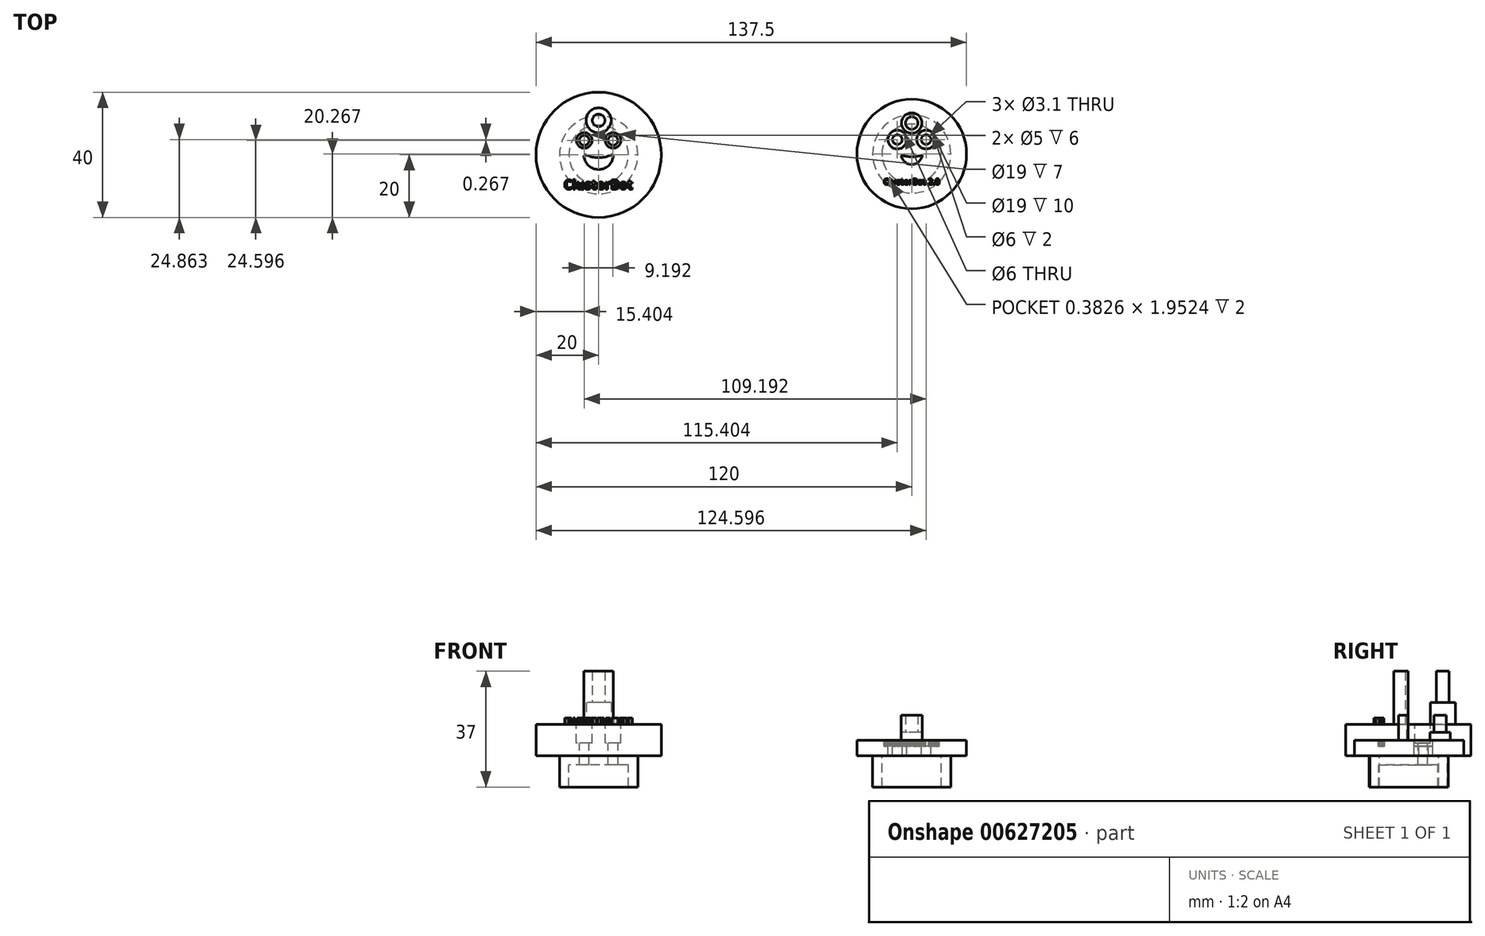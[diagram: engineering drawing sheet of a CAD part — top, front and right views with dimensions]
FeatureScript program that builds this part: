
annotation { "Feature Type Name" : "Feature", "Feature Type Description" : "" }
export const myFeature = defineFeature(function(context is Context, id is Id, definition is map)
    precondition{}
    {
        {
            var Q0;
            Q0=qCreatedBy(makeId("Top.planeOp"),FACE);
            var sketch = newSketch(context, id + "F0", { "sketchPlane" : qUnion([Q0])});
            skCircle(sketch, "E0", {"center": v(0, 0) * mm, "radius": 20 * mm});
            skLineSegment(sketch, "E1", {"start": v(0, 57.86) * mm, "end": v(0, -51.25) * mm, "construction": true});
            skLineSegment(sketch, "E2", {"start": v(-57.98, 0) * mm, "end": v(50.32, 0) * mm, "construction": true});
            skCircle(sketch, "E3", {"center": v(0, 11) * mm, "radius": 2 * mm});
            skCircle(sketch, "E4", {"center": v(0, 0) * mm, "radius": 4.7 * mm});
            skLineSegment(sketch, "E5", {"start": v(0, 11) * mm, "end": v(0, 0) * mm});
            skLineSegment(sketch, "E6", {"start": v(0, 36.77) * mm, "end": v(-4.7, 0.27) * mm, "construction": true});
            skCircle(sketch, "E7", {"center": v(0, 0) * mm, "radius": 9.5 * mm});
            skCircle(sketch, "E8", {"center": v(0, 0) * mm, "radius": 12.5 * mm});
            skArc(sketch, "E9", {"start": v(-4.7, 0.27) * mm, "mid": v(0, -0.9) * mm, "end": v(4.7, 0.27) * mm});
            skLineSegment(sketch, "E10", {"start": v(50, 46.01) * mm, "end": v(50, -53.99) * mm, "construction": true});
            skCircle(sketch, "E11", {"center": v(100, 0.27) * mm, "radius": 9.5 * mm});
            skCircle(sketch, "E12", {"center": v(100, 0.27) * mm, "radius": 12.5 * mm});
            skLineSegment(sketch, "E13", {"start": v(100, 0.27) * mm, "end": v(100, 40.45) * mm, "construction": true});
            skCircle(sketch, "E14", {"center": v(100, 10.14) * mm, "radius": 2 * mm});
            skCircle(sketch, "E15", {"center": v(100, 0.27) * mm, "radius": 17.5 * mm});
            skCircle(sketch, "E16", {"center": v(100, 0.27) * mm, "radius": 3.37 * mm});
            skLineSegment(sketch, "E17", {"start": v(96.65, -0.12) * mm, "end": v(103.35, -0.12) * mm});
            skArc(sketch, "E18", {"start": v(96.65, -0.12) * mm, "mid": v(100, -0.6) * mm, "end": v(103.35, -0.12) * mm});
            skSolve(sketch);
        }
        {
            var Q0;
            Q0=makeQuery(id+"F0.imprint","IMPRINT",FACE,{"disambiguationData":[TD([[makeQuery(id+"F0.imprint","IMPRINT",EDGE,{"derivedFrom":sQuery(id+"F0.wireOp",EDGE,"E0")}),1.0]])]});
            var Q1;
            {var subQ0=sQuery(id+"F0.wireOp",EDGE,"EMk8Hpbs-Uu9s-4hnP-Wr23-4mz9YGDRhDCW");var subQ1=sQuery(id+"F0.wireOp",EDGE,"E4");var subQ2=makeQuery(id+"F0.imprint","INTERSECT",VERTEX,{"disambiguationData":[OD(0.0)],"derivedFrom":[subQ1,subQ0]});Q1=makeQuery(id+"F0.imprint","IMPRINT",FACE,{"disambiguationData":[TD([[makeQuery(id+"F0.imprint","IMPRINT",EDGE,{"disambiguationData":[TD([[subQ2,1.0]])],"derivedFrom":subQ1}),1.0]])]});}
            var Q2;
            {var subQ0=sQuery(id+"F0.wireOp",EDGE,"EMk8Hpbs-Uu9s-4hnP-Wr23-4mz9YGDRhDCW");var subQ1=sQuery(id+"F0.wireOp",EDGE,"E4");var subQ2=makeQuery(id+"F0.imprint","INTERSECT",VERTEX,{"disambiguationData":[OD(1.0)],"derivedFrom":[subQ1,subQ0]});Q2=makeQuery(id+"F0.imprint","IMPRINT",FACE,{"disambiguationData":[TD([[makeQuery(id+"F0.imprint","IMPRINT",EDGE,{"disambiguationData":[TD([[subQ2,-1.0]])],"derivedFrom":subQ1}),1.0]])]});}
            var Q3;
            {var subQ3=sQuery(id+"F0.wireOp",EDGE,"E5");var subQ6=sQuery(id+"F0.wireOp",EDGE,"E3");var subQ7=makeQuery(id+"F0.imprint","INTERSECT",VERTEX,{"derivedFrom":[subQ6,subQ3]});Q3=makeQuery(id+"F0.imprint","IMPRINT",FACE,{"disambiguationData":[TD([[makeQuery(id+"F0.imprint","IMPRINT",EDGE,{"disambiguationData":[TD([[subQ7,1.0]])],"derivedFrom":subQ6}),-1.0]])]});}
            extrude(context, id + "F1", {"entities" : qUnion([Q0, Q1, Q2, Q3]), "depth" : 10 * mm, "offsetDistance" : 25 * mm});
        }
        {
            var Q0;
            Q0=makeQuery(id+"F0.imprint","IMPRINT",FACE,{"disambiguationData":[TD([[makeQuery(id+"F0.imprint","IMPRINT",EDGE,{"derivedFrom":sQuery(id+"F0.wireOp",EDGE,"E3")}),1.0]])]});
            var Q1;
            {var subQ0=sQuery(id+"F0.wireOp",EDGE,"EMk8Hpbs-Uu9s-4hnP-Wr23-4mz9YGDRhDCW");var subQ1=sQuery(id+"F0.wireOp",EDGE,"E4");var subQ2=makeQuery(id+"F0.imprint","INTERSECT",VERTEX,{"disambiguationData":[OD(0.0)],"derivedFrom":[subQ1,subQ0]});Q1=makeQuery(id+"F0.imprint","IMPRINT",FACE,{"disambiguationData":[TD([[makeQuery(id+"F0.imprint","IMPRINT",EDGE,{"disambiguationData":[TD([[subQ2,-1.0]])],"derivedFrom":subQ1}),1.0]])]});}
            var Q2;
            {var subQ0=sQuery(id+"F0.wireOp",EDGE,"E8");var subQ1=sQuery(id+"F0.wireOp",EDGE,"E3");var subQ2=makeQuery(id+"F0.imprint","INTERSECT",VERTEX,{"disambiguationData":[OD(0.0)],"derivedFrom":[subQ1,subQ0]});Q2=makeQuery(id+"F0.imprint","IMPRINT",FACE,{"disambiguationData":[TD([[makeQuery(id+"F0.imprint","IMPRINT",EDGE,{"disambiguationData":[TD([[subQ2,1.0]])],"derivedFrom":subQ1}),1.0]])]});}
            var Q3;
            {var subQ0=sQuery(id+"F0.wireOp",EDGE,"E5");var subQ1=sQuery(id+"F0.wireOp",EDGE,"E3");var subQ2=makeQuery(id+"F0.imprint","INTERSECT",VERTEX,{"derivedFrom":[subQ1,subQ0]});Q3=makeQuery(id+"F0.imprint","IMPRINT",FACE,{"disambiguationData":[TD([[makeQuery(id+"F0.imprint","IMPRINT",EDGE,{"disambiguationData":[TD([[subQ2,-1.0]])],"derivedFrom":subQ1}),1.0]])]});}
            var Q4;
            {var subQ0=sQuery(id+"F0.wireOp",EDGE,"E5");var subQ1=sQuery(id+"F0.wireOp",EDGE,"E3");var subQ2=makeQuery(id+"F0.imprint","INTERSECT",VERTEX,{"derivedFrom":[subQ1,subQ0]});Q4=makeQuery(id+"F0.imprint","IMPRINT",FACE,{"disambiguationData":[TD([[makeQuery(id+"F0.imprint","IMPRINT",EDGE,{"disambiguationData":[TD([[subQ2,1.0]])],"derivedFrom":subQ1}),1.0]])]});}
            extrude(context, id + "F2", {"entities" : qUnion([Q0, Q1, Q2, Q3, Q4]), "operationType" : NewBodyOperationType.ADD, "depth" : 27 * mm, "offsetDistance" : 25 * mm});
        }
        {
            var Q0;
            {var subQ0=sQuery(id+"F0.wireOp",EDGE,"E8");var subQ1=sQuery(id+"F0.wireOp",EDGE,"E3");var subQ2=makeQuery(id+"F0.imprint","INTERSECT",VERTEX,{"disambiguationData":[OD(0.0)],"derivedFrom":[subQ1,subQ0]});Q0=makeQuery(id+"F0.imprint","IMPRINT",FACE,{"disambiguationData":[TD([[makeQuery(id+"F0.imprint","IMPRINT",EDGE,{"disambiguationData":[TD([[subQ2,-1.0]])],"derivedFrom":subQ1}),-1.0]])]});}
            extrude(context, id + "F3", {"entities" : qUnion([Q0]), "operationType" : NewBodyOperationType.ADD, "oppositeDirection" : true, "depth" : 10 * mm, "offsetDistance" : 25 * mm, "hasSecondDirection" : true, "secondDirectionOppositeDirection" : false, "secondDirectionDepth" : 10 * mm});
        }
        {
            var Q0;
            {var subQ2=sQuery(id+"F0.wireOp",EDGE,"E3");var subQ5=sQuery(id+"F0.wireOp",EDGE,"E8");var subQ6=makeQuery(id+"F0.imprint","INTERSECT",VERTEX,{"disambiguationData":[OD(0.0)],"derivedFrom":[subQ2,subQ5]});Q0=makeQuery(id+"F0.imprint","IMPRINT",FACE,{"disambiguationData":[TD([[makeQuery(id+"F0.imprint","IMPRINT",EDGE,{"disambiguationData":[TD([[subQ6,-1.0]])],"derivedFrom":subQ2}),1.0]])]});}
            extrude(context, id + "F4", {"entities" : qUnion([Q0]), "operationType" : NewBodyOperationType.ADD, "oppositeDirection" : true, "depth" : 10 * mm, "offsetDistance" : 25 * mm});
        }
        {
            var Q0;
            {var subQ0=sQuery(id+"F0.wireOp",EDGE,"E9");var subQ1=sQuery(id+"F0.wireOp",EDGE,"E4");Q0=makeQuery(id+"F2.opExtrude","SWEPT_EDGE",EDGE,{"disambiguationData":[OSD([subQ1,subQ0]),TDD([makeQuery(id+"F0.imprint","INTERSECT",VERTEX,{"disambiguationData":[OD(1.0)],"derivedFrom":[subQ1,subQ0]})])]});}
            var Q1;
            {var subQ0=sQuery(id+"F0.wireOp",EDGE,"E9");var subQ1=sQuery(id+"F0.wireOp",EDGE,"E4");Q1=makeQuery(id+"F2.opExtrude","SWEPT_EDGE",EDGE,{"disambiguationData":[OSD([subQ1,subQ0]),TDD([makeQuery(id+"F0.imprint","INTERSECT",VERTEX,{"disambiguationData":[OD(0.0)],"derivedFrom":[subQ1,subQ0]})])]});}
            fillet(context, id + "F5", {"entities" : qUnion([Q0, Q1]), "radius" : 0.5 * mm, "tangentPropagation" : true, "allowEdgeOverflow" : false});
        }
        {
            var Q0;
            {var subQ0=sQuery(id+"F0.wireOp",EDGE,"E8");var subQ1=sQuery(id+"F0.wireOp",EDGE,"E7");var subQ2=sQuery(id+"F0.wireOp",EDGE,"E3");Q0=makeQuery(id+"F3.boolean.opBoolean","MERGE",FACE,{"derivedFrom":[makeQuery(id+"F1.opExtrude","CAP_FACE",FACE,{"disambiguationData":[OSD([sQuery(id+"F0.wireOp",EDGE,"E0"),subQ2,subQ0])],"isStart":false}),makeQuery(id+"F1.opExtrude","CAP_FACE",FACE,{"disambiguationData":[OSD([subQ2,sQuery(id+"F0.wireOp",EDGE,"E4"),subQ1,sQuery(id+"F0.wireOp",EDGE,"E9")])],"isStart":false}),makeQuery(id+"F3.opExtrude","CAP_FACE",FACE,{"disambiguationData":[OSD([subQ2,subQ1,subQ0])],"isStart":true})]});}
            var sketch = newSketch(context, id + "F6", { "sketchPlane" : qUnion([Q0])});
            skLineSegment(sketch, "E19", {"start": v(0, 0) * mm, "end": v(-10.6, 10.6) * mm, "construction": true});
            skLineSegment(sketch, "E20", {"start": v(0, 0) * mm, "end": v(10.6, 10.6) * mm, "construction": true});
            skCircle(sketch, "E21", {"center": v(4.6, 4.6) * mm, "radius": 1.55 * mm});
            skCircle(sketch, "E22", {"center": v(4.6, 4.6) * mm, "radius": 2.5 * mm});
            skCircle(sketch, "E23", {"center": v(-4.6, 4.6) * mm, "radius": 1.55 * mm});
            skCircle(sketch, "E24", {"center": v(-4.6, 4.6) * mm, "radius": 2.5 * mm});
            skSolve(sketch);
        }
        {
            var Q0;
            Q0=makeQuery(id+"F6.imprint","IMPRINT",FACE,{"disambiguationData":[TD([[makeQuery(id+"F6.imprint","IMPRINT",EDGE,{"derivedFrom":sQuery(id+"F6.wireOp",EDGE,"E23")}),1.0]])]});
            var Q1;
            Q1=makeQuery(id+"F6.imprint","IMPRINT",FACE,{"disambiguationData":[TD([[makeQuery(id+"F6.imprint","IMPRINT",EDGE,{"derivedFrom":sQuery(id+"F6.wireOp",EDGE,"E21")}),1.0]])]});
            extrude(context, id + "F7", {"entities" : qUnion([Q0, Q1]), "operationType" : NewBodyOperationType.REMOVE, "oppositeDirection" : true, "depth" : 10 * mm, "offsetDistance" : 25 * mm});
        }
        {
            var Q0;
            Q0=makeQuery(id+"F6.imprint","IMPRINT",FACE,{"disambiguationData":[TD([[makeQuery(id+"F6.imprint","IMPRINT",EDGE,{"derivedFrom":sQuery(id+"F6.wireOp",EDGE,"E21")}),-1.0]])]});
            var Q1;
            Q1=makeQuery(id+"F6.imprint","IMPRINT",FACE,{"disambiguationData":[TD([[makeQuery(id+"F6.imprint","IMPRINT",EDGE,{"derivedFrom":sQuery(id+"F6.wireOp",EDGE,"E23")}),-1.0]])]});
            extrude(context, id + "F8", {"entities" : qUnion([Q0, Q1]), "operationType" : NewBodyOperationType.REMOVE, "oppositeDirection" : true, "depth" : 6 * mm, "offsetDistance" : 25 * mm});
        }
        {
            var Q0;
            {var subQ0=sQuery(id+"F0.wireOp",EDGE,"E8");var subQ1=sQuery(id+"F0.wireOp",EDGE,"E7");var subQ2=sQuery(id+"F0.wireOp",EDGE,"E3");Q0=makeQuery(id+"F3.boolean.opBoolean","MERGE",FACE,{"derivedFrom":[makeQuery(id+"F1.opExtrude","CAP_FACE",FACE,{"disambiguationData":[OSD([sQuery(id+"F0.wireOp",EDGE,"E0"),subQ2,subQ0])],"isStart":false}),makeQuery(id+"F1.opExtrude","CAP_FACE",FACE,{"disambiguationData":[OSD([subQ2,sQuery(id+"F0.wireOp",EDGE,"E4"),subQ1,sQuery(id+"F0.wireOp",EDGE,"E9")])],"isStart":false}),makeQuery(id+"F3.opExtrude","CAP_FACE",FACE,{"disambiguationData":[OSD([subQ2,subQ1,subQ0])],"isStart":true})]});}
            var sketch = newSketch(context, id + "F9", { "sketchPlane" : qUnion([Q0])});
            skText(sketch, "E25", { "text": "ClusterBot", "fontName": "OpenSans-Bold.ttf"});
            const initialGuessF9  = {"E25": [-0.01111, -0.011, 1, 0, 0.003]};
            skSetInitialGuess(sketch, initialGuessF9);
            skSolve(sketch);
        }
        {
            var Q0;
            Q0=qSketchRegion(id+"F9",true);
            extrude(context, id + "F10", {"entities" : qUnion([Q0]), "operationType" : NewBodyOperationType.ADD, "depth" : 2 * mm, "offsetDistance" : 25 * mm});
        }
        {
            var Q0;
            {var subQ0=sQuery(id+"F0.wireOp",EDGE,"E9");var subQ1=sQuery(id+"F0.wireOp",EDGE,"E4");var subQ2=sQuery(id+"F0.wireOp",EDGE,"E3");var subQ3=sQuery(id+"F0.wireOp",EDGE,"E0");var subQ4=sQuery(id+"F0.wireOp",EDGE,"E8");var subQ5=sQuery(id+"F0.wireOp",EDGE,"E7");Q0=makeQuery(id+"F10.boolean.opBoolean","SPLIT",FACE,{"disambiguationData":[TD([makeQuery(id+"F1.opExtrude","SWEPT_FACE",FACE,{"disambiguationData":[OSD([subQ3])]})])],"derivedFrom":makeQuery(id+"F3.boolean.opBoolean","MERGE",FACE,{"derivedFrom":[makeQuery(id+"F1.opExtrude","CAP_FACE",FACE,{"disambiguationData":[OSD([subQ3,subQ2,subQ4])],"isStart":false}),makeQuery(id+"F1.opExtrude","CAP_FACE",FACE,{"disambiguationData":[OSD([subQ2,subQ1,subQ5,subQ0])],"isStart":false}),makeQuery(id+"F3.opExtrude","CAP_FACE",FACE,{"disambiguationData":[OSD([subQ2,subQ5,subQ4])],"isStart":true})]})});}
            var sketch = newSketch(context, id + "F11", { "sketchPlane" : qUnion([Q0])});
            skCircle(sketch, "E26", {"center": v(0, 11) * mm, "radius": 4 * mm});
            skSolve(sketch);
        }
        {
            var Q0;
            Q0=qSketchRegion(id+"F11",true);
            extrude(context, id + "F12", {"entities" : qUnion([Q0]), "operationType" : NewBodyOperationType.ADD, "depth" : 7 * mm, "offsetDistance" : 25 * mm});
        }
        {
            var Q0;
            {var subQ0=sQuery(id+"F0.wireOp",EDGE,"E7");var subQ1=sQuery(id+"F0.wireOp",EDGE,"E9");var subQ2=sQuery(id+"F0.wireOp",EDGE,"E4");var subQ3=sQuery(id+"F0.wireOp",EDGE,"E3");Q0=makeQuery(id+"F4.boolean.opBoolean","SPLIT",FACE,{"disambiguationData":[TD([makeQuery(id+"F3.opExtrude","SWEPT_FACE",FACE,{"disambiguationData":[OSD([subQ0])]})])],"derivedFrom":makeQuery(id+"F2.boolean.opBoolean","MERGE",FACE,{"derivedFrom":[makeQuery(id+"F1.opExtrude","CAP_FACE",FACE,{"disambiguationData":[OSD([sQuery(id+"F0.wireOp",EDGE,"E0"),subQ3,sQuery(id+"F0.wireOp",EDGE,"E8")])],"isStart":true}),makeQuery(id+"F1.opExtrude","CAP_FACE",FACE,{"disambiguationData":[OSD([subQ3,subQ2,subQ0,subQ1])],"isStart":true}),makeQuery(id+"F2.opExtrude","CAP_FACE",FACE,{"disambiguationData":[OSD([subQ3])],"isStart":true}),makeQuery(id+"F2.opExtrude","CAP_FACE",FACE,{"disambiguationData":[OSD([subQ2,subQ1])],"isStart":true})]})});}
            extrude(context, id + "F13", {"entities" : qUnion([Q0]), "operationType" : NewBodyOperationType.ADD, "depth" : 3 * mm, "offsetDistance" : 25 * mm});
        }
        {
            var Q0;
            Q0=makeQuery(id+"F0.imprint","IMPRINT",FACE,{"disambiguationData":[TD([[makeQuery(id+"F0.imprint","IMPRINT",EDGE,{"derivedFrom":sQuery(id+"F0.wireOp",EDGE,"E12")}),-1.0]])]});
            var Q1;
            Q1=makeQuery(id+"F0.imprint","IMPRINT",FACE,{"disambiguationData":[TD([[makeQuery(id+"F0.imprint","IMPRINT",EDGE,{"derivedFrom":sQuery(id+"F0.wireOp",EDGE,"E12")}),1.0]])]});
            var Q2;
            {var subQ0=sQuery(id+"F0.wireOp",EDGE,"E14");var subQ1=sQuery(id+"F0.wireOp",EDGE,"E11");var subQ2=makeQuery(id+"F0.imprint","INTERSECT",VERTEX,{"disambiguationData":[OD(0.0)],"derivedFrom":[subQ1,subQ0]});Q2=makeQuery(id+"F0.imprint","IMPRINT",FACE,{"disambiguationData":[TD([[makeQuery(id+"F0.imprint","IMPRINT",EDGE,{"disambiguationData":[TD([[subQ2,-1.0]])],"derivedFrom":subQ1}),1.0]])]});}
            var Q3;
            {var subQ0=sQuery(id+"F0.wireOp",EDGE,"INGHYkTo-cHFD-LJoG-0GR1-I3Dc0VJQrvcC");Q3=makeQuery(id+"F0.imprint","IMPRINT",FACE,{"disambiguationData":[TD([[makeQuery(id+"F0.imprint","IMPRINT",EDGE,{"derivedFrom":subQ0}),1.0]])]});}
            var Q4;
            {var subQ0=sQuery(id+"F0.wireOp",EDGE,"hYN0OAPL-6847-LTPc-NbCf-sZvM7d4d9N3J");Q4=makeQuery(id+"F0.imprint","IMPRINT",FACE,{"disambiguationData":[TD([[makeQuery(id+"F0.imprint","IMPRINT",EDGE,{"derivedFrom":subQ0}),1.0]])]});}
            var Q5;
            {var subQ1=sQuery(id+"F0.wireOp",EDGE,"E17");Q5=makeQuery(id+"F0.imprint","IMPRINT",FACE,{"disambiguationData":[TD([[makeQuery(id+"F0.imprint","IMPRINT",EDGE,{"derivedFrom":subQ1}),1.0]])]});}
            var Q6;
            Q6=makeQuery(id+"F0.imprint","IMPRINT",FACE,{"disambiguationData":[TD([[makeQuery(id+"F0.imprint","IMPRINT",EDGE,{"derivedFrom":sQuery(id+"F0.wireOp",EDGE,"E17")}),-1.0]])]});
            extrude(context, id + "F14", {"entities" : qUnion([Q0, Q1, Q2, Q3, Q4, Q5, Q6]), "depth" : 5 * mm, "offsetDistance" : 25 * mm});
        }
        {
            var Q0;
            {var subQ0=sQuery(id+"F0.wireOp",EDGE,"E14");var subQ1=sQuery(id+"F0.wireOp",EDGE,"E11");var subQ2=makeQuery(id+"F0.imprint","INTERSECT",VERTEX,{"disambiguationData":[OD(0.0)],"derivedFrom":[subQ1,subQ0]});Q0=makeQuery(id+"F0.imprint","IMPRINT",FACE,{"disambiguationData":[TD([[makeQuery(id+"F0.imprint","IMPRINT",EDGE,{"disambiguationData":[TD([[subQ2,1.0]])],"derivedFrom":subQ1}),-1.0]])]});}
            var Q1;
            {var subQ0=sQuery(id+"F0.wireOp",EDGE,"E14");var subQ1=sQuery(id+"F0.wireOp",EDGE,"E11");var subQ2=makeQuery(id+"F0.imprint","INTERSECT",VERTEX,{"disambiguationData":[OD(0.0)],"derivedFrom":[subQ1,subQ0]});Q1=makeQuery(id+"F0.imprint","IMPRINT",FACE,{"disambiguationData":[TD([[makeQuery(id+"F0.imprint","IMPRINT",EDGE,{"disambiguationData":[TD([[subQ2,1.0]])],"derivedFrom":subQ1}),1.0]])]});}
            var Q2;
            {var subQ0=sQuery(id+"F0.wireOp",EDGE,"hYN0OAPL-6847-LTPc-NbCf-sZvM7d4d9N3J");Q2=makeQuery(id+"F0.imprint","IMPRINT",FACE,{"disambiguationData":[TD([[makeQuery(id+"F0.imprint","IMPRINT",EDGE,{"derivedFrom":subQ0}),-1.0]])]});}
            var Q3;
            {var subQ0=sQuery(id+"F0.wireOp",EDGE,"E18");Q3=makeQuery(id+"F0.imprint","IMPRINT",FACE,{"disambiguationData":[TD([[makeQuery(id+"F0.imprint","IMPRINT",EDGE,{"derivedFrom":subQ0}),-1.0]])]});}
            extrude(context, id + "F15", {"entities" : qUnion([Q0, Q1, Q2, Q3]), "operationType" : NewBodyOperationType.ADD, "depth" : 13 * mm, "offsetDistance" : 25 * mm});
        }
        {
            var Q0;
            Q0=makeQuery(id+"F0.imprint","IMPRINT",FACE,{"disambiguationData":[TD([[makeQuery(id+"F0.imprint","IMPRINT",EDGE,{"derivedFrom":sQuery(id+"F0.wireOp",EDGE,"E12")}),1.0]])]});
            var Q1;
            {var subQ0=sQuery(id+"F0.wireOp",EDGE,"E14");var subQ1=sQuery(id+"F0.wireOp",EDGE,"E11");var subQ2=makeQuery(id+"F0.imprint","INTERSECT",VERTEX,{"disambiguationData":[OD(0.0)],"derivedFrom":[subQ1,subQ0]});Q1=makeQuery(id+"F0.imprint","IMPRINT",FACE,{"disambiguationData":[TD([[makeQuery(id+"F0.imprint","IMPRINT",EDGE,{"disambiguationData":[TD([[subQ2,1.0]])],"derivedFrom":subQ1}),-1.0]])]});}
            extrude(context, id + "F16", {"entities" : qUnion([Q0, Q1]), "operationType" : NewBodyOperationType.ADD, "oppositeDirection" : true, "depth" : 10 * mm, "offsetDistance" : 25 * mm});
        }
        {
            var Q0;
            Q0=makeQuery(id+"F14.opExtrude","CAP_FACE",FACE,{"disambiguationData":[OSD([sQuery(id+"F0.wireOp",EDGE,"E14"),sQuery(id+"F0.wireOp",EDGE,"E15"),sQuery(id+"F0.wireOp",EDGE,"E16"),sQuery(id+"F0.wireOp",EDGE,"INGHYkTo-cHFD-LJoG-0GR1-I3Dc0VJQrvcC")])],"isStart":false});
            var sketch = newSketch(context, id + "F17", { "sketchPlane" : qUnion([Q0])});
            skLineSegment(sketch, "E27", {"start": v(100, 0.27) * mm, "end": v(108.49, 8.75) * mm, "construction": true});
            skLineSegment(sketch, "E28", {"start": v(100, 0.27) * mm, "end": v(91.51, 8.75) * mm, "construction": true});
            skCircle(sketch, "E29", {"center": v(104.6, 4.86) * mm, "radius": 1.55 * mm});
            skCircle(sketch, "E30", {"center": v(104.6, 4.86) * mm, "radius": 3 * mm});
            skLineSegment(sketch, "E31", {"start": v(100, 0.27) * mm, "end": v(100, 10.14) * mm, "construction": true});
            skCircle(sketch, "E32.MirrorC", {"center": v(95.4, 4.86) * mm, "radius": 1.55 * mm});
            skCircle(sketch, "E33.MirrorC", {"center": v(95.4, 4.86) * mm, "radius": 3 * mm});
            skCircle(sketch, "E34", {"center": v(100, 10.14) * mm, "radius": 3.25 * mm});
            skSolve(sketch);
        }
        {
            var Q0;
            Q0=makeQuery(id+"F17.imprint","IMPRINT",FACE,{"disambiguationData":[TD([[makeQuery(id+"F17.imprint","IMPRINT",EDGE,{"derivedFrom":sQuery(id+"F17.wireOp",EDGE,"E32.MirrorC")}),1.0]])]});
            var Q1;
            Q1=makeQuery(id+"F17.imprint","IMPRINT",FACE,{"disambiguationData":[TD([[makeQuery(id+"F17.imprint","IMPRINT",EDGE,{"derivedFrom":sQuery(id+"F17.wireOp",EDGE,"E29")}),-1.0]])]});
            extrude(context, id + "F18", {"entities" : qUnion([Q0, Q1]), "operationType" : NewBodyOperationType.REMOVE, "oppositeDirection" : true, "depth" : 2 * mm, "offsetDistance" : 25 * mm});
        }
        {
            var Q0;
            Q0=makeQuery(id+"F17.imprint","IMPRINT",FACE,{"disambiguationData":[TD([[makeQuery(id+"F17.imprint","IMPRINT",EDGE,{"derivedFrom":sQuery(id+"F17.wireOp",EDGE,"E32.MirrorC")}),-1.0]])]});
            var Q1;
            Q1=makeQuery(id+"F17.imprint","IMPRINT",FACE,{"disambiguationData":[TD([[makeQuery(id+"F17.imprint","IMPRINT",EDGE,{"derivedFrom":sQuery(id+"F17.wireOp",EDGE,"E29")}),1.0]])]});
            extrude(context, id + "F19", {"entities" : qUnion([Q0, Q1]), "operationType" : NewBodyOperationType.REMOVE, "oppositeDirection" : true, "depth" : 10 * mm, "offsetDistance" : 25 * mm});
        }
        {
            var Q0;
            {var subQ0=sQuery(id+"F0.wireOp",EDGE,"INGHYkTo-cHFD-LJoG-0GR1-I3Dc0VJQrvcC");var subQ1=sQuery(id+"F0.wireOp",EDGE,"E16");var subQ2=sQuery(id+"F0.wireOp",EDGE,"E14");var subQ3=sQuery(id+"F0.wireOp",EDGE,"E15");Q0=makeQuery(id+"F18.boolean.opBoolean","SPLIT",FACE,{"disambiguationData":[TD([makeQuery(id+"F14.opExtrude","SWEPT_FACE",FACE,{"disambiguationData":[OSD([subQ3])]})])],"derivedFrom":makeQuery(id+"F14.opExtrude","CAP_FACE",FACE,{"disambiguationData":[OSD([subQ2,subQ3,subQ1,subQ0])],"isStart":false})});}
            var sketch = newSketch(context, id + "F20", { "sketchPlane" : qUnion([Q0])});
            skText(sketch, "E35", { "text": "ClusterBot 2.0", "fontName": "OpenSans-Bold.ttf"});
            const initialGuessF20  = {"E35": [0.091, -0.0095, 1, 0, 0.00185]};
            skSetInitialGuess(sketch, initialGuessF20);
            skSolve(sketch);
        }
        {
            var Q0;
            Q0 = qSketchRegion(id + "F20", true);
            extrude(context, id + "F21", {"entities" : qUnion([Q0]), "operationType" : NewBodyOperationType.REMOVE, "oppositeDirection" : true, "depth" : 2 * mm, "offsetDistance" : 25 * mm});
        }
        {
            var Q0;
            Q0=makeQuery(id+"F17.imprint","IMPRINT",FACE,{"disambiguationData":[TD([[makeQuery(id+"F17.imprint","IMPRINT",EDGE,{"derivedFrom":sQuery(id+"F17.wireOp",EDGE,"E34")}),1.0]])]});
            extrude(context, id + "F22", {"entities" : qUnion([Q0]), "operationType" : NewBodyOperationType.ADD, "depth" : 2.5 * mm, "offsetDistance" : 25 * mm});
        }
    });
